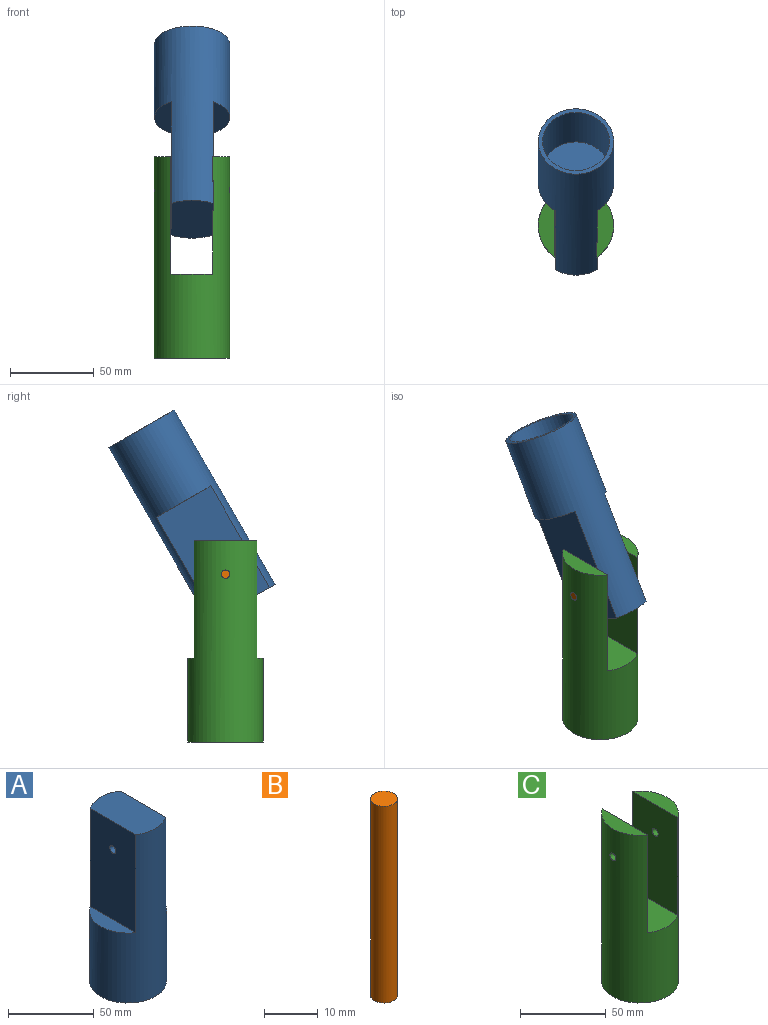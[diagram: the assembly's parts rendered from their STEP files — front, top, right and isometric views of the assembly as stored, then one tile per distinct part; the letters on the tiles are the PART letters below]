
ASSEMBLY  parts=3 mates=2
PART A: 10 faces, bbox 45x45x120 mm
  f0: plane 45x25mm, normal (0,0,1), area 1064.1mm2, adj f1,f3,f5
  f1: cylinder r=22.5mm len=120mm, axis (0,0,-1), area 10779.5mm2, adj f0,f2,f3,f4,f5,f6
  f2: plane 45x45mm, normal (0,0,-1), area 333.8mm2, adj f1,f7
  f3: plane 70x37.42mm, normal (1,0,0), area 2599.5mm2, adj f0,f1,f4,f9
  f4: plane 37.42x10mm, normal (0,0,1), area 263.2mm2, adj f1,f3
  f5: plane 70x37.42mm, normal (-1,0,0), area 2599.5mm2, adj f0,f1,f6,f9
  f6: plane 37.42x10mm, normal (0,0,1), area 263.2mm2, adj f1,f5
  f7: cylinder r=20mm len=40mm, axis (0,0,-1), area 4398.2mm2, adj f2,f8
  f8: plane 40x40mm, normal (0,0,-1), area 1256.6mm2, adj f7
  f9: cylinder r=2.5mm len=25mm, axis (1,0,0), area 392.7mm2, adj f3,f5
PART B: 3 faces, bbox 5x5x45 mm
  f0: cylinder r=2.5mm len=45mm, axis (0,0,-1), area 706.9mm2, adj f1,f2
  f1: plane 5x5mm, normal (0,0,1), area 19.6mm2, adj f0
  f2: plane 5x5mm, normal (0,0,-1), area 19.6mm2, adj f0
PART C: 11 faces, bbox 45x45x120 mm
  f0: cylinder r=22.5mm len=120mm, axis (0,0,-1), area 13214.5mm2, adj f1,f2,f3,f4,f5,f6,f9,f10
  f1: plane 37.42x10mm, normal (0,0,1), area 263.2mm2, adj f0,f4
  f2: plane 37.42x10mm, normal (0,0,1), area 263.2mm2, adj f0,f5
  f3: plane 45x45mm, normal (0,0,-1), area 333.8mm2, adj f0,f7
  f4: plane 70x37.42mm, normal (-1,0,0), area 2599.5mm2, adj f0,f1,f6,f10
  f5: plane 70x37.42mm, normal (1,0,0), area 2599.5mm2, adj f0,f2,f6,f9
  f6: plane 45x25mm, normal (0,0,1), area 1064.1mm2, adj f0,f4,f5
  f7: cylinder r=20mm len=40mm, axis (0,0,-1), area 4398.2mm2, adj f3,f8
  f8: plane 40x40mm, normal (0,0,-1), area 1256.6mm2, adj f7
  f9: cylinder r=2.5mm len=10mm, axis (1,0,0), area 156mm2, adj f0,f5
  f10: cylinder r=2.5mm len=10mm, axis (1,0,0), area 156mm2, adj f0,f4
PLACE A rot(axis=(1,0,0),150deg) t=(-51.9,47.16,167.34)mm
PLACE B rot(axis=(0,1,0),90deg) t=(-74.4,-2.84,80.74)mm
PLACE C t=(-51.96,-2.84,-19.26)mm fixed
MATE fastened C.f9 <-> B.f0  axis (1,0,0) through (-29.4,-2.84,80.74)mm
MATE revolute A.f9 <-> B.f0  axis (1,0,0) through (-51.9,-2.84,80.74)mm
